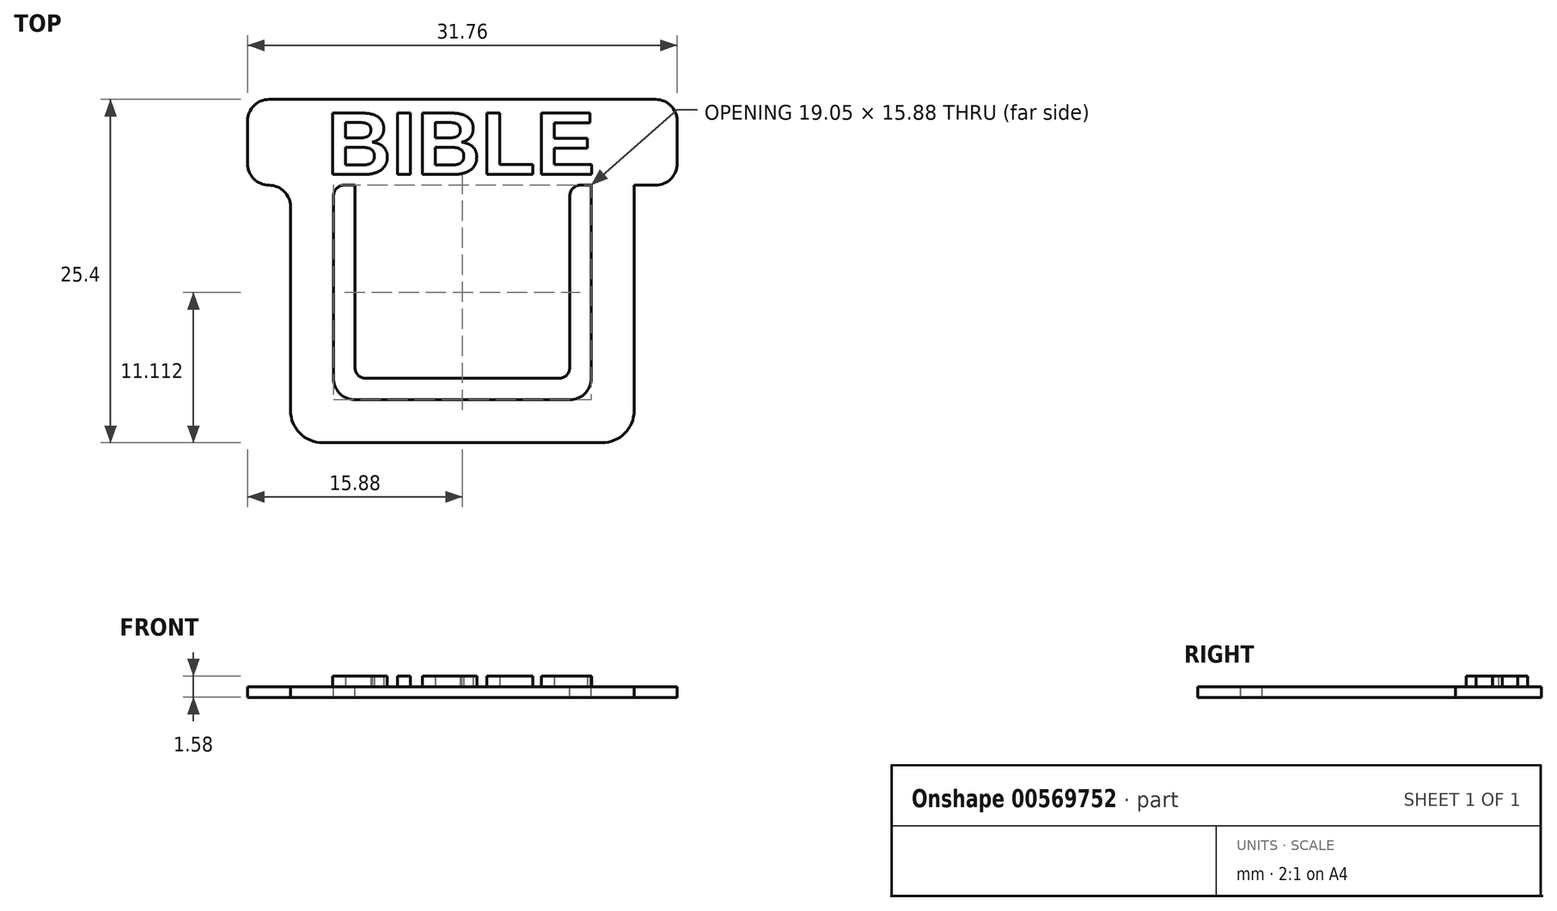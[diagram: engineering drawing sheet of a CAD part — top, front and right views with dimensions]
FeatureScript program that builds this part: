
annotation { "Feature Type Name" : "Feature", "Feature Type Description" : "" }
export const myFeature = defineFeature(function(context is Context, id is Id, definition is map)
    precondition{}
    {
        {
            var Q0;
            Q0=qCreatedBy(makeId("Front.planeOp"),FACE);
            var sketch = newSketch(context, id + "F0", { "sketchPlane" : qUnion([Q0])});
            skLineSegment(sketch, "E0.bottom", {"start": v(12.7, 9.53) * mm, "end": v(-12.7, 9.53) * mm});
            skLineSegment(sketch, "E0.top", {"start": v(12.7, -9.53) * mm, "end": v(-12.7, -9.53) * mm});
            skLineSegment(sketch, "E0.left", {"start": v(12.7, 9.53) * mm, "end": v(12.7, -9.53) * mm});
            skLineSegment(sketch, "E0.right", {"start": v(-12.7, 9.53) * mm, "end": v(-12.7, -9.53) * mm});
            skPoint(sketch, "E0.middle", {"position": v(0, 0) * mm});
            skSolve(sketch);
        }
        {
            var Q0;
            Q0=makeQuery(id+"F0.imprint","IMPRINT",FACE,{"disambiguationData":[TD([[makeQuery(id+"F0.imprint","IMPRINT",EDGE,{"derivedFrom":sQuery(id+"F0.wireOp",EDGE,"E0.bottom")}),1.0]])]});
            extrude(context, id + "F1", {"entities" : qUnion([Q0]), "depth" : 0.8 * mm, "offsetDistance" : 25.4 * mm});
        }
        {
            var Q0;
            Q0=makeQuery(id+"F1.opExtrude","SWEPT_EDGE",EDGE,{"disambiguationData":[OSD([sQuery(id+"F0.wireOp",EDGE,"E0.top"),sQuery(id+"F0.wireOp",EDGE,"E0.left")])]});
            var Q1;
            Q1=makeQuery(id+"F1.opExtrude","SWEPT_EDGE",EDGE,{"disambiguationData":[OSD([sQuery(id+"F0.wireOp",EDGE,"E0.top"),sQuery(id+"F0.wireOp",EDGE,"E0.right")])]});
            fillet(context, id + "F2", {"entities" : qUnion([Q0, Q1]), "radius" : 2.38 * mm, "tangentPropagation" : true, "allowEdgeOverflow" : false});
        }
        {
            var Q0;
            Q0=makeQuery(id+"F1.opExtrude","CAP_FACE",FACE,{"disambiguationData":[OSD([sQuery(id+"F0.wireOp",EDGE,"E0.bottom"),sQuery(id+"F0.wireOp",EDGE,"E0.top"),sQuery(id+"F0.wireOp",EDGE,"E0.left"),sQuery(id+"F0.wireOp",EDGE,"E0.right")])],"isStart":false});
            var sketch = newSketch(context, id + "F3", { "sketchPlane" : qUnion([Q0])});
            skLineSegment(sketch, "E1.bottom", {"start": v(9.52, 9.53) * mm, "end": v(-9.53, 9.53) * mm});
            skLineSegment(sketch, "E1.top", {"start": v(9.53, -6.35) * mm, "end": v(-9.53, -6.35) * mm});
            skLineSegment(sketch, "E1.left", {"start": v(9.52, 9.53) * mm, "end": v(9.53, -6.35) * mm});
            skLineSegment(sketch, "E1.right", {"start": v(-9.53, 9.53) * mm, "end": v(-9.52, -6.35) * mm});
            skPoint(sketch, "E1.middle", {"position": v(0, 0) * mm});
            skSolve(sketch);
        }
        {
            var Q0;
            Q0=makeQuery(id+"F3.imprint","IMPRINT",FACE,{"disambiguationData":[TD([[makeQuery(id+"F3.imprint","IMPRINT",EDGE,{"derivedFrom":sQuery(id+"F3.wireOp",EDGE,"E1.bottom")}),1.0]])]});
            extrude(context, id + "F4", {"entities" : qUnion([Q0]), "operationType" : NewBodyOperationType.REMOVE, "oppositeDirection" : true, "depth" : 4.93 * mm, "offsetDistance" : 25.4 * mm});
        }
        {
            var Q0;
            Q0=makeQuery(id+"F1.opExtrude","CAP_FACE",FACE,{"disambiguationData":[OSD([sQuery(id+"F0.wireOp",EDGE,"E0.bottom"),sQuery(id+"F0.wireOp",EDGE,"E0.top"),sQuery(id+"F0.wireOp",EDGE,"E0.left"),sQuery(id+"F0.wireOp",EDGE,"E0.right")])],"isStart":false});
            var sketch = newSketch(context, id + "F5", { "sketchPlane" : qUnion([Q0])});
            skLineSegment(sketch, "E2.bottom", {"start": v(-15.88, 9.53) * mm, "end": v(15.87, 9.53) * mm});
            skLineSegment(sketch, "E2.top", {"start": v(-15.88, 15.88) * mm, "end": v(15.87, 15.88) * mm});
            skLineSegment(sketch, "E2.left", {"start": v(-15.88, 9.53) * mm, "end": v(-15.88, 15.88) * mm});
            skLineSegment(sketch, "E2.right", {"start": v(15.87, 9.53) * mm, "end": v(15.87, 15.88) * mm});
            skSolve(sketch);
        }
        {
            var Q0;
            Q0=makeQuery(id+"F5.imprint","IMPRINT",FACE,{"disambiguationData":[TD([[makeQuery(id+"F5.imprint","IMPRINT",EDGE,{"derivedFrom":sQuery(id+"F5.wireOp",EDGE,"E2.top")}),-1.0]])]});
            extrude(context, id + "F6", {"entities" : qUnion([Q0]), "operationType" : NewBodyOperationType.ADD, "oppositeDirection" : true, "depth" : 0.8 * mm, "offsetDistance" : 25.4 * mm});
        }
        {
            var Q0;
            Q0=makeQuery(id+"F6.opExtrude","SWEPT_EDGE",EDGE,{"disambiguationData":[OSD([sQuery(id+"F5.wireOp",EDGE,"E2.top"),sQuery(id+"F5.wireOp",EDGE,"E2.left")])]});
            var Q1;
            Q1=makeQuery(id+"F6.opExtrude","SWEPT_EDGE",EDGE,{"disambiguationData":[OSD([sQuery(id+"F5.wireOp",EDGE,"E2.top"),sQuery(id+"F5.wireOp",EDGE,"E2.right")])]});
            var Q2;
            Q2=makeQuery(id+"F6.opExtrude","SWEPT_EDGE",EDGE,{"disambiguationData":[OSD([sQuery(id+"F5.wireOp",EDGE,"E2.bottom"),sQuery(id+"F5.wireOp",EDGE,"E2.right")])]});
            var Q3;
            Q3=makeQuery(id+"F1.opExtrude","SWEPT_EDGE",EDGE,{"disambiguationData":[OSD([sQuery(id+"F0.wireOp",EDGE,"E0.bottom"),sQuery(id+"F0.wireOp",EDGE,"E0.left")])]});
            var Q4;
            Q4=makeQuery(id+"F6.opExtrude","SWEPT_EDGE",EDGE,{"disambiguationData":[OSD([sQuery(id+"F5.wireOp",EDGE,"E2.bottom"),sQuery(id+"F5.wireOp",EDGE,"E2.left")])]});
            var Q5;
            Q5=makeQuery(id+"F1.opExtrude","SWEPT_EDGE",EDGE,{"disambiguationData":[OSD([sQuery(id+"F0.wireOp",EDGE,"E0.bottom"),sQuery(id+"F0.wireOp",EDGE,"E0.right")])]});
            fillet(context, id + "F7", {"entities" : qUnion([Q0, Q1, Q2, Q3, Q4, Q5]), "radius" : 1.59 * mm, "tangentPropagation" : true, "allowEdgeOverflow" : false});
        }
        {
            var Q0;
            Q0=makeQuery(id+"F4.boolean.opBoolean","COPY",EDGE,{"derivedFrom":makeQuery(id+"F4.opExtrude","SWEPT_EDGE",EDGE,{"disambiguationData":[OSD([sQuery(id+"F3.wireOp",EDGE,"E1.top"),sQuery(id+"F3.wireOp",EDGE,"E1.right")])]})});
            var Q1;
            Q1=makeQuery(id+"F4.boolean.opBoolean","COPY",EDGE,{"derivedFrom":makeQuery(id+"F4.opExtrude","SWEPT_EDGE",EDGE,{"disambiguationData":[OSD([sQuery(id+"F3.wireOp",EDGE,"E1.top"),sQuery(id+"F3.wireOp",EDGE,"E1.left")])]})});
            fillet(context, id + "F8", {"entities" : qUnion([Q0, Q1]), "radius" : 1.59 * mm, "tangentPropagation" : true, "allowEdgeOverflow" : false});
        }
        {
            var Q0;
            Q0=makeQuery(id+"F6.boolean.opBoolean","MERGE",FACE,{"derivedFrom":[makeQuery(id+"F1.opExtrude","CAP_FACE",FACE,{"disambiguationData":[OSD([sQuery(id+"F0.wireOp",EDGE,"E0.bottom"),sQuery(id+"F0.wireOp",EDGE,"E0.top"),sQuery(id+"F0.wireOp",EDGE,"E0.left"),sQuery(id+"F0.wireOp",EDGE,"E0.right")])],"isStart":false}),makeQuery(id+"F6.opExtrude","CAP_FACE",FACE,{"disambiguationData":[OSD([sQuery(id+"F5.wireOp",EDGE,"E2.bottom"),sQuery(id+"F5.wireOp",EDGE,"E2.top"),sQuery(id+"F5.wireOp",EDGE,"E2.left"),sQuery(id+"F5.wireOp",EDGE,"E2.right")])],"isStart":true})]});
            var sketch = newSketch(context, id + "F9", { "sketchPlane" : qUnion([Q0])});
            skLineSegment(sketch, "E3.bottom", {"start": v(-7.94, 9.53) * mm, "end": v(7.94, 9.53) * mm});
            skLineSegment(sketch, "E3.top", {"start": v(-7.94, -4.76) * mm, "end": v(7.94, -4.76) * mm});
            skLineSegment(sketch, "E3.left", {"start": v(-7.94, 9.53) * mm, "end": v(-7.94, -4.76) * mm});
            skLineSegment(sketch, "E3.right", {"start": v(7.94, 9.53) * mm, "end": v(7.94, -4.76) * mm});
            skSolve(sketch);
        }
        {
            var Q0;
            Q0=makeQuery(id+"F9.imprint","IMPRINT",FACE,{"disambiguationData":[TD([[makeQuery(id+"F9.imprint","IMPRINT",EDGE,{"derivedFrom":sQuery(id+"F9.wireOp",EDGE,"E3.bottom")}),1.0]])]});
            extrude(context, id + "F10", {"entities" : qUnion([Q0]), "operationType" : NewBodyOperationType.ADD, "oppositeDirection" : true, "depth" : 0.8 * mm, "offsetDistance" : 25.4 * mm});
        }
        {
            var Q0;
            Q0=makeQuery(id+"F10.boolean.opBoolean","MERGE",FACE,{"derivedFrom":[makeQuery(id+"F6.boolean.opBoolean","MERGE",FACE,{"derivedFrom":[makeQuery(id+"F1.opExtrude","CAP_FACE",FACE,{"disambiguationData":[OSD([sQuery(id+"F0.wireOp",EDGE,"E0.bottom"),sQuery(id+"F0.wireOp",EDGE,"E0.top"),sQuery(id+"F0.wireOp",EDGE,"E0.left"),sQuery(id+"F0.wireOp",EDGE,"E0.right")])],"isStart":false}),makeQuery(id+"F6.opExtrude","CAP_FACE",FACE,{"disambiguationData":[OSD([sQuery(id+"F5.wireOp",EDGE,"E2.bottom"),sQuery(id+"F5.wireOp",EDGE,"E2.top"),sQuery(id+"F5.wireOp",EDGE,"E2.left"),sQuery(id+"F5.wireOp",EDGE,"E2.right")])],"isStart":true})]}),makeQuery(id+"F10.opExtrude","CAP_FACE",FACE,{"disambiguationData":[OSD([sQuery(id+"F9.wireOp",EDGE,"E3.bottom"),sQuery(id+"F9.wireOp",EDGE,"E3.top"),sQuery(id+"F9.wireOp",EDGE,"E3.left"),sQuery(id+"F9.wireOp",EDGE,"E3.right")])],"isStart":true})]});
            var sketch = newSketch(context, id + "F11", { "sketchPlane" : qUnion([Q0])});
            skText(sketch, "E4", { "text": "BIBLE", "fontName": "Arimo-Bold.ttf"});
            const initialGuessF11  = {"E4": [-0.01002, 0.01032, 1, 0, 0.00476]};
            skSetInitialGuess(sketch, initialGuessF11);
            skSolve(sketch);
        }
        {
            var Q0;
            Q0=qSketchRegion(id+"F11",true);
            extrude(context, id + "F12", {"entities" : qUnion([Q0]), "operationType" : NewBodyOperationType.ADD, "depth" : 0.8 * mm, "offsetDistance" : 25.4 * mm});
        }
        {
            var Q0;
            Q0=makeQuery(id+"F10.opExtrude","SWEPT_EDGE",EDGE,{"disambiguationData":[OSD([sQuery(id+"F5.wireOp",EDGE,"E2.bottom"),sQuery(id+"F9.wireOp",EDGE,"E3.bottom"),sQuery(id+"F9.wireOp",EDGE,"E3.left")])]});
            var Q1;
            Q1=makeQuery(id+"F4.boolean.opBoolean","COPY",EDGE,{"derivedFrom":makeQuery(id+"F4.opExtrude","SWEPT_EDGE",EDGE,{"disambiguationData":[OSD([sQuery(id+"F0.wireOp",EDGE,"E0.bottom"),sQuery(id+"F3.wireOp",EDGE,"E1.bottom"),sQuery(id+"F3.wireOp",EDGE,"E1.right")])]})});
            var Q2;
            Q2=makeQuery(id+"F10.opExtrude","SWEPT_EDGE",EDGE,{"disambiguationData":[OSD([sQuery(id+"F5.wireOp",EDGE,"E2.bottom"),sQuery(id+"F9.wireOp",EDGE,"E3.bottom"),sQuery(id+"F9.wireOp",EDGE,"E3.right")])]});
            var Q3;
            Q3=makeQuery(id+"F4.boolean.opBoolean","COPY",EDGE,{"derivedFrom":makeQuery(id+"F4.opExtrude","SWEPT_EDGE",EDGE,{"disambiguationData":[OSD([sQuery(id+"F0.wireOp",EDGE,"E0.bottom"),sQuery(id+"F3.wireOp",EDGE,"E1.bottom"),sQuery(id+"F3.wireOp",EDGE,"E1.left")])]})});
            fillet(context, id + "F13", {"entities" : qUnion([Q0, Q1, Q2, Q3]), "radius" : 0.8 * mm, "tangentPropagation" : true, "allowEdgeOverflow" : false});
        }
        {
            var Q0;
            Q0=makeQuery(id+"F10.opExtrude","SWEPT_EDGE",EDGE,{"disambiguationData":[OSD([sQuery(id+"F9.wireOp",EDGE,"E3.top"),sQuery(id+"F9.wireOp",EDGE,"E3.left")])]});
            var Q1;
            Q1=makeQuery(id+"F10.opExtrude","SWEPT_EDGE",EDGE,{"disambiguationData":[OSD([sQuery(id+"F9.wireOp",EDGE,"E3.top"),sQuery(id+"F9.wireOp",EDGE,"E3.right")])]});
            fillet(context, id + "F14", {"entities" : qUnion([Q0, Q1]), "radius" : 0.8 * mm, "tangentPropagation" : true, "allowEdgeOverflow" : false});
        }
        {
            var Q0;
            Q0=makeQuery(id+"F1.opExtrude","SWEPT_BODY",BODY,{"disambiguationData":[OSD([sQuery(id+"F0.wireOp",EDGE,"E0.bottom"),sQuery(id+"F0.wireOp",EDGE,"E0.top"),sQuery(id+"F0.wireOp",EDGE,"E0.left"),sQuery(id+"F0.wireOp",EDGE,"E0.right")])]});
            var Q1;
            Q1=makeQuery(id+"F6.opExtrude","CAP_EDGE",EDGE,{"disambiguationData":[OSD([sQuery(id+"F5.wireOp",EDGE,"E2.top")])],"isStart":false});
            transform(context, id + "F15", {"entities" : qUnion([Q0]), "transformType" : TransformType.ROTATION, "transformAxis" : qUnion([Q1]), "angle" : 270 * degree, "makeCopy" : false});
        }
    });
